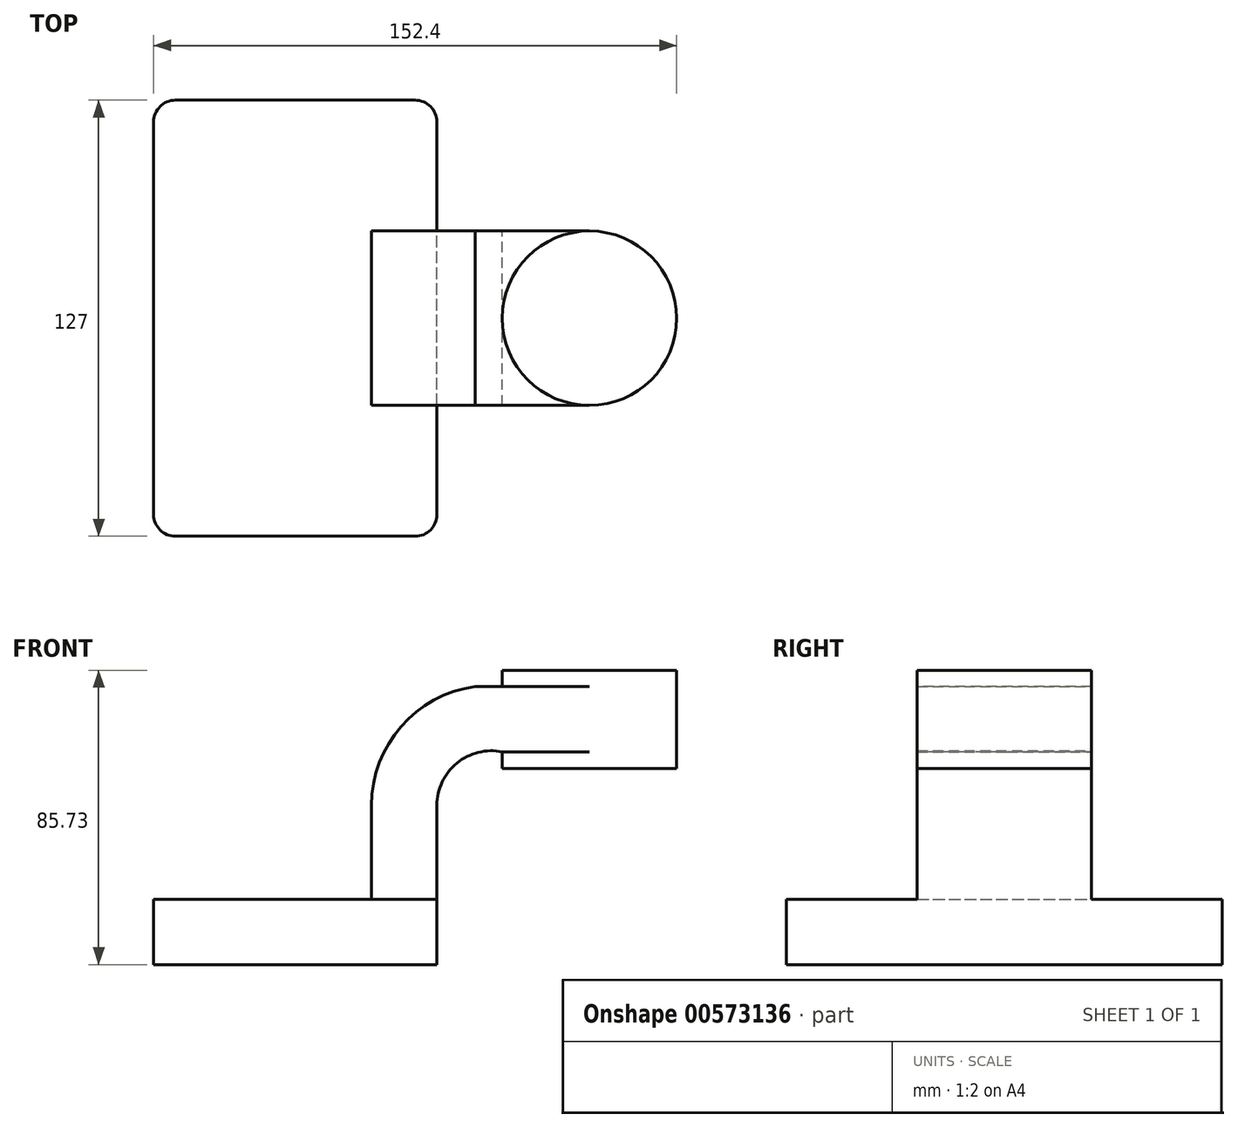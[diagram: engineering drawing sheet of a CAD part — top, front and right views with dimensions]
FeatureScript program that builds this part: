
annotation { "Feature Type Name" : "Feature", "Feature Type Description" : "" }
export const myFeature = defineFeature(function(context is Context, id is Id, definition is map)
    precondition{}
    {
        {
            var Q0;
            Q0=qCreatedBy(makeId("Front.planeOp"),FACE);
            var sketch = newSketch(context, id + "F0", { "sketchPlane" : qUnion([Q0])});
            skLineSegment(sketch, "E0.bottom", {"start": v(-41.27, -9.53) * mm, "end": v(41.28, -9.53) * mm});
            skLineSegment(sketch, "E0.top", {"start": v(-41.28, 9.53) * mm, "end": v(41.27, 9.53) * mm});
            skLineSegment(sketch, "E0.left", {"start": v(-41.27, -9.53) * mm, "end": v(-41.28, 9.53) * mm});
            skLineSegment(sketch, "E0.right", {"start": v(41.28, -9.53) * mm, "end": v(41.27, 9.53) * mm});
            skPoint(sketch, "E0.middle", {"position": v(0, 0) * mm});
            skLineSegment(sketch, "E1", {"start": v(41.27, 9.53) * mm, "end": v(41.27, 36.85) * mm});
            skLineSegment(sketch, "E2.bottom", {"start": v(60.33, 47.63) * mm, "end": v(111.12, 47.63) * mm});
            skLineSegment(sketch, "E2.top", {"start": v(60.33, 76.2) * mm, "end": v(111.12, 76.2) * mm});
            skLineSegment(sketch, "E2.left", {"start": v(60.33, 47.63) * mm, "end": v(60.33, 76.2) * mm});
            skLineSegment(sketch, "E2.right", {"start": v(111.12, 47.63) * mm, "end": v(111.12, 76.2) * mm});
            skPoint(sketch, "E2.middle", {"position": v(85.72, 61.91) * mm});
            skArc(sketch, "E3", {"start": v(41.27, 36.85) * mm, "mid": v(47.12, 49.15) * mm, "end": v(60.34, 52.4) * mm});
            skLineSegment(sketch, "E4", {"start": v(60.34, 52.4) * mm, "end": v(85.72, 52.4) * mm});
            skPoint(sketch, "E5.endSnap0", {"position": v(85.72, 47.63) * mm});
            skLineSegment(sketch, "E6.0", {"start": v(52.4, 71.45) * mm, "end": v(85.72, 71.45) * mm});
            skArc(sketch, "E6.1", {"start": v(22.22, 36.85) * mm, "mid": v(30.83, 59.8) * mm, "end": v(52.4, 71.45) * mm});
            skLineSegment(sketch, "E6.2", {"start": v(22.22, 9.53) * mm, "end": v(22.22, 36.85) * mm});
            skLineSegment(sketch, "E7", {"start": v(85.72, 71.45) * mm, "end": v(85.72, 47.63) * mm});
            skFitSpline(sketch, "E8", {"points": [v(-41.28, 9.53) * mm, v(52.4, 71.45) * mm], "startDerivative": vector(6.14, 113.2) * mm, "endDerivative": vector(120.04, 11.54) * mm});
            skLineSegment(sketch, "E9", {"start": v(85.72, 71.45) * mm, "end": v(85.72, 76.2) * mm});
            skSolve(sketch);
        }
        {
            var Q0;
            Q0=makeQuery(id+"F0.imprint","IMPRINT",FACE,{"disambiguationData":[TD([[makeQuery(id+"F0.imprint","IMPRINT",EDGE,{"derivedFrom":sQuery(id+"F0.wireOp",EDGE,"E0.bottom")}),1.0]])]});
            extrude(context, id + "F1", {"entities" : qUnion([Q0]), "endBound" : BoundingType.SYMMETRIC, "depth" : 127 * mm, "offsetDistance" : 25.4 * mm});
        }
        {
            var Q0;
            {var subQ1=sQuery(id+"F0.wireOp",EDGE,"E1");Q0=makeQuery(id+"F0.imprint","IMPRINT",FACE,{"disambiguationData":[TD([[makeQuery(id+"F0.imprint","IMPRINT",EDGE,{"derivedFrom":subQ1}),1.0]])]});}
            extrude(context, id + "F2", {"entities" : qUnion([Q0]), "operationType" : NewBodyOperationType.ADD, "endBound" : BoundingType.SYMMETRIC, "depth" : 50.8 * mm, "offsetDistance" : 25.4 * mm});
        }
        {
            var Q0;
            Q0=makeQuery(id+"F0.imprint","IMPRINT",FACE,{"disambiguationData":[TD([[makeQuery(id+"F0.imprint","IMPRINT",EDGE,{"derivedFrom":sQuery(id+"F0.wireOp",EDGE,"E6.1")}),1.0]])]});
            extrude(context, id + "F3", {"entities" : qUnion([Q0]), "operationType" : NewBodyOperationType.ADD, "endBound" : BoundingType.SYMMETRIC, "depth" : 15.88 * mm, "offsetDistance" : 25.4 * mm});
        }
        {
            var Q0;
            {var subQ5=sQuery(id+"F0.wireOp",EDGE,"E4");Q0=makeQuery(id+"F0.imprint","IMPRINT",FACE,{"disambiguationData":[TD([[makeQuery(id+"F0.imprint","IMPRINT",EDGE,{"derivedFrom":subQ5}),1.0]])]});}
            extrude(context, id + "F4", {"entities" : qUnion([Q0]), "operationType" : NewBodyOperationType.ADD, "endBound" : BoundingType.SYMMETRIC, "depth" : 50.8 * mm, "offsetDistance" : 25.4 * mm});
        }
        {
            var Q0;
            {var subQ3=sQuery(id+"F0.wireOp",EDGE,"E2.right");Q0=makeQuery(id+"F0.imprint","IMPRINT",FACE,{"disambiguationData":[TD([[makeQuery(id+"F0.imprint","IMPRINT",EDGE,{"derivedFrom":subQ3}),1.0]])]});}
            var Q1;
            Q1=sQuery(id+"F0.wireOp",EDGE,"E7");
            revolve(context, id + "F5", {"operationType" : NewBodyOperationType.ADD, "entities" : qUnion([Q0]), "axis" : qUnion([Q1]), "revolveType" : RevolveType.FULL});
        }
        {
            var Q0;
            Q0=makeQuery(id+"F1.opExtrude","CAP_EDGE",EDGE,{"disambiguationData":[OSD([sQuery(id+"F0.wireOp",EDGE,"E0.right")])],"isStart":false});
            var Q1;
            Q1=makeQuery(id+"F1.opExtrude","CAP_EDGE",EDGE,{"disambiguationData":[OSD([sQuery(id+"F0.wireOp",EDGE,"E0.right")])],"isStart":true});
            var Q2;
            Q2=makeQuery(id+"F1.opExtrude","CAP_EDGE",EDGE,{"disambiguationData":[OSD([sQuery(id+"F0.wireOp",EDGE,"E0.left")])],"isStart":false});
            var Q3;
            Q3=makeQuery(id+"F1.opExtrude","CAP_EDGE",EDGE,{"disambiguationData":[OSD([sQuery(id+"F0.wireOp",EDGE,"E0.left")])],"isStart":true});
            fillet(context, id + "F6", {"entities" : qUnion([Q0, Q1, Q2, Q3]), "radius" : 6.35 * mm, "tangentPropagation" : true, "allowEdgeOverflow" : false});
        }
    });
